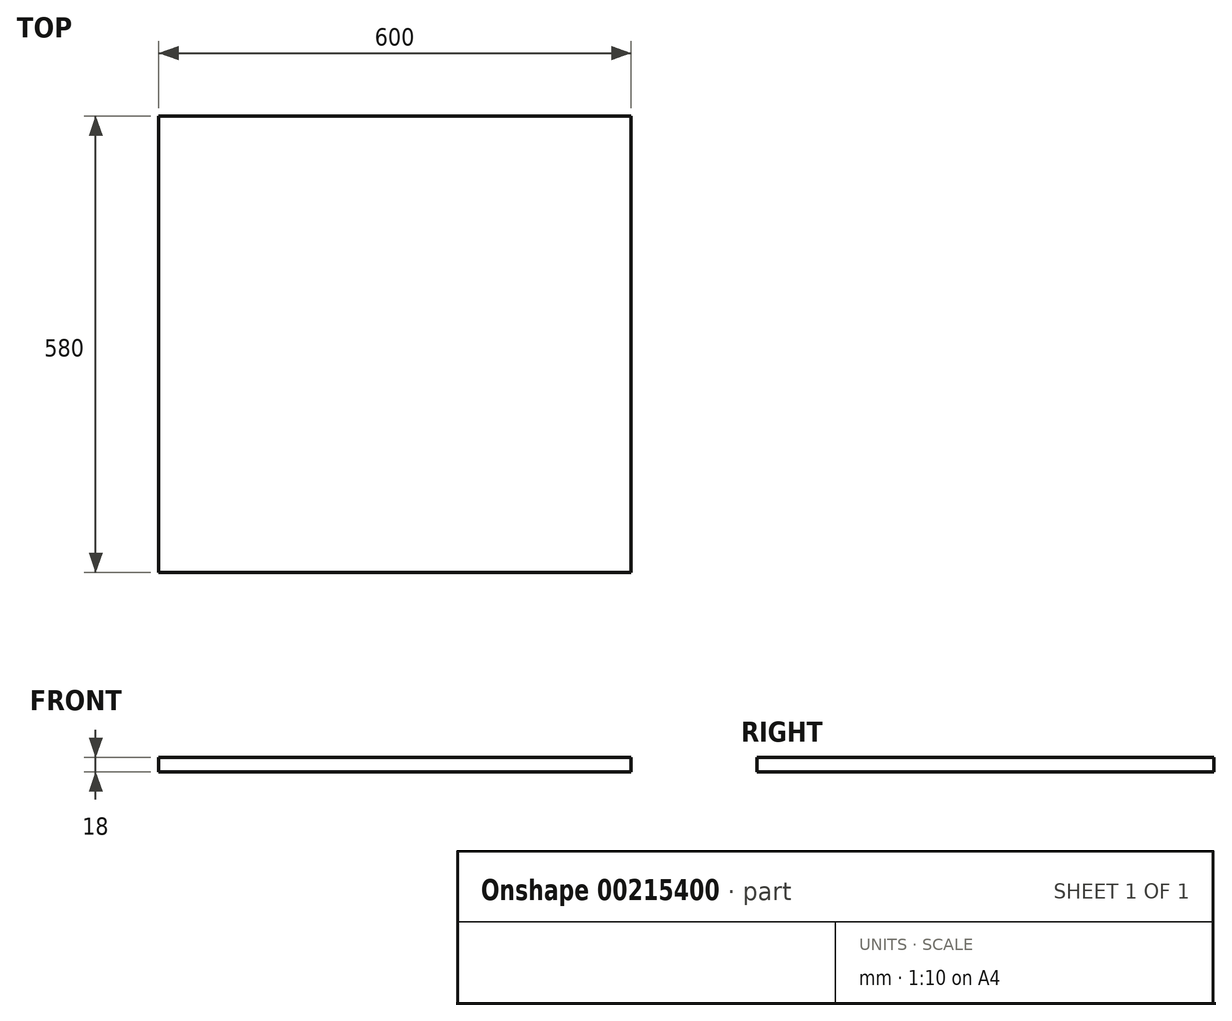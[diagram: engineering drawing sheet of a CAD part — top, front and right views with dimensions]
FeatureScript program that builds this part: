
annotation { "Feature Type Name" : "Feature", "Feature Type Description" : "" }
export const myFeature = defineFeature(function(context is Context, id is Id, definition is map)
    precondition{}
    {
        {
            var Q0;
            Q0=qCreatedBy(makeId("Top.planeOp"),FACE);
            var sketch = newSketch(context, id + "F0", { "sketchPlane" : qUnion([Q0])});
            skLineSegment(sketch, "E0.bottom", {"start": v(-300, 290) * mm, "end": v(300, 290) * mm});
            skLineSegment(sketch, "E0.top", {"start": v(-300, -290) * mm, "end": v(300, -290) * mm});
            skLineSegment(sketch, "E0.left", {"start": v(-300, 290) * mm, "end": v(-300, -290) * mm});
            skLineSegment(sketch, "E0.right", {"start": v(300, 290) * mm, "end": v(300, -290) * mm});
            skPoint(sketch, "E0.middle", {"position": v(0, 0) * mm});
            skSolve(sketch);
        }
        {
            var Q0;
            Q0=makeQuery(id+"F0.imprint","IMPRINT",FACE,{"disambiguationData":[TD([[makeQuery(id+"F0.imprint","IMPRINT",EDGE,{"derivedFrom":sQuery(id+"F0.wireOp",EDGE,"E0.bottom")}),-1.0]])]});
            extrude(context, id + "F1", {"entities" : qUnion([Q0]), "depth" : 18 * mm});
        }
    });
